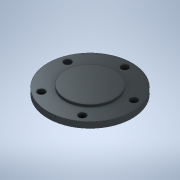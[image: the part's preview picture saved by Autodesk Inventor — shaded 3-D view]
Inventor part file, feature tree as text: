
AUTODESK INVENTOR PART (.ipt)
format: ipt  version: 2020 (Build 240168000, 168)  size: 134,144 bytes
history: native  units: mm
features: extrude x4, sketch x4
ambient origin geometry x8: Origin, YZ Plane, XZ Plane, XY Plane, X Axis, Y Axis, Z Axis, Center Point
bodies: Solid1 (feature_tree)
feature tree (8):
  extrude  "Extrusion1"  Depth=2.5mm TaperAngle=0.0deg
  extrude  "Extrusion2"  Depth=1.0mm TaperAngle=0.0deg
  extrude  "Extrusion3"  Depth=0.5mm TaperAngle=0.0deg
  extrude  "Extrusion4"  Depth=3.0mm
  sketch  "Sketch1"  dims[d0=35.0mm d1=2.5mm d2=0.0mm]
  sketch  "Sketch2"  dims[d3=20.5mm d4=1.0mm d5=0.0mm]
  sketch  "Sketch3"  dims[d6=19.0mm d7=0.5mm d8=0.0mm]
  sketch  "Sketch4"  dims[d9=3.0mm d10=14.5mm d11=50.0mm d13=360.0deg d15=0.0mm d16=0.0mm]
